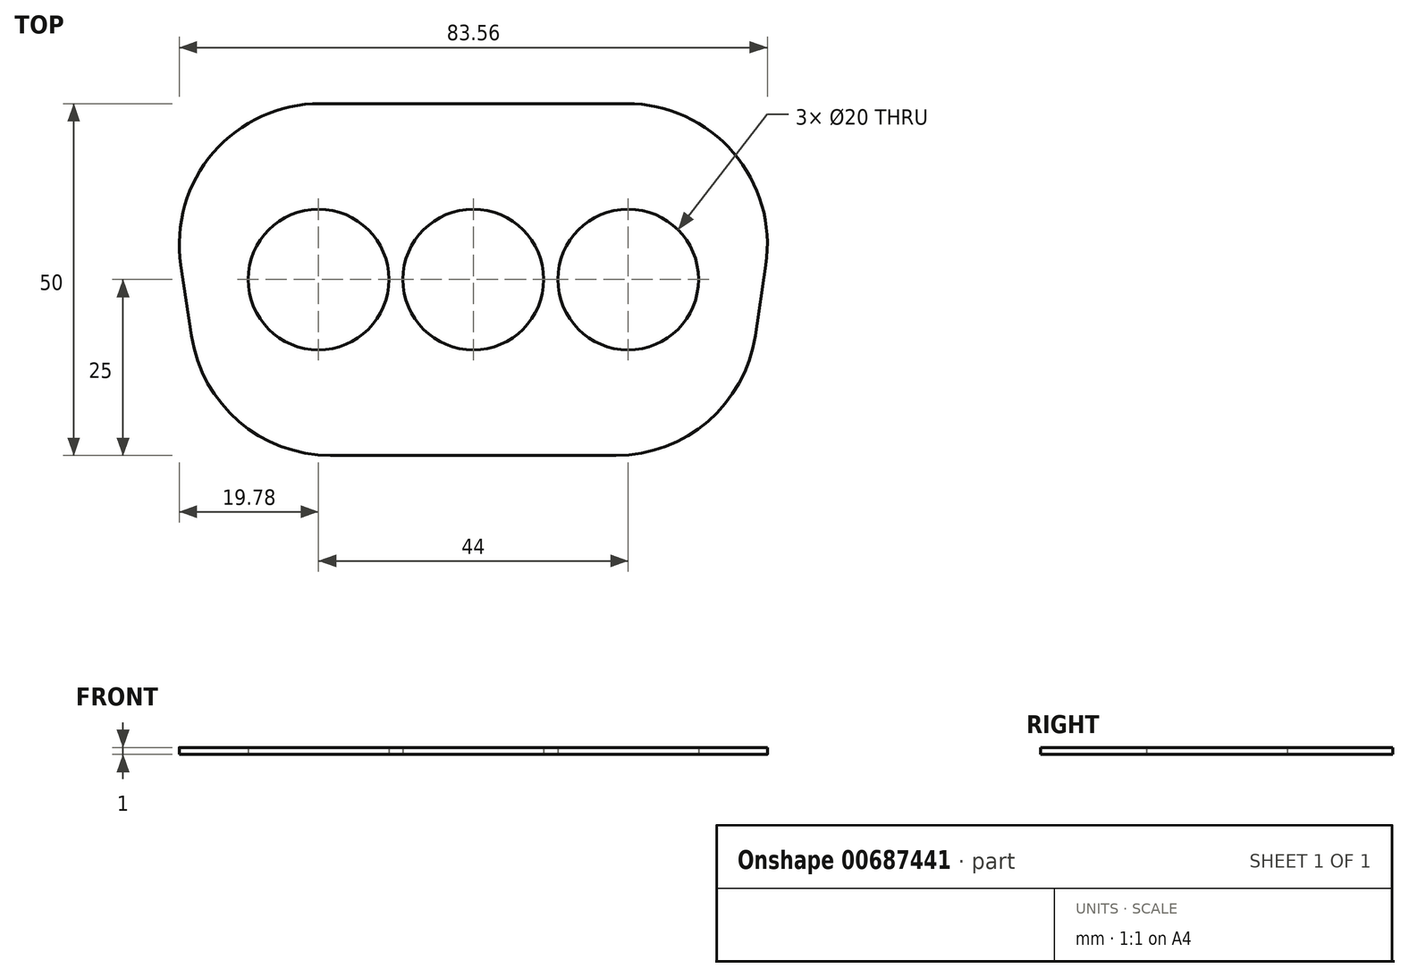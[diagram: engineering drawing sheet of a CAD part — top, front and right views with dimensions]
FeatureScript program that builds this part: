
annotation { "Feature Type Name" : "Feature", "Feature Type Description" : "" }
export const myFeature = defineFeature(function(context is Context, id is Id, definition is map)
    precondition{}
    {
        {
            var Q0;
            Q0=qCreatedBy(makeId("Top.planeOp"),FACE);
            var sketch = newSketch(context, id + "F0", { "sketchPlane" : qUnion([Q0])});
            skLineSegment(sketch, "E0", {"start": v(-45, 0) * mm, "end": v(45, 0) * mm});
            skLineSegment(sketch, "E1", {"start": v(-37.5, -50) * mm, "end": v(37.5, -50) * mm});
            skLineSegment(sketch, "E2", {"start": v(0, 0) * mm, "end": v(0, -50) * mm});
            skLineSegment(sketch, "E3", {"start": v(-45, 0) * mm, "end": v(-37.5, -50) * mm});
            skLineSegment(sketch, "E4", {"start": v(37.5, -50) * mm, "end": v(45, 0) * mm});
            skCircle(sketch, "E5", {"center": v(0, -25) * mm, "radius": 10 * mm});
            skCircle(sketch, "E6", {"center": v(-22, -25) * mm, "radius": 10 * mm});
            skCircle(sketch, "E7.MirrorC", {"center": v(22, -25) * mm, "radius": 10 * mm});
            skSolve(sketch);
        }
        {
            var Q0;
            Q0 = qSketchRegion(id + "F0", true);
            extrude(context, id + "F1", {"entities" : qUnion([Q0]), "depth" : 1 * mm, "offsetDistance" : 25 * mm});
        }
        {
            var Q0;
            Q0=makeQuery(id+"F1.opExtrude","SWEPT_EDGE",EDGE,{"disambiguationData":[OSD([sQuery(id+"F0.wireOp",EDGE,"E1"),sQuery(id+"F0.wireOp",EDGE,"E3")])]});
            var Q1;
            Q1=makeQuery(id+"F1.opExtrude","SWEPT_EDGE",EDGE,{"disambiguationData":[OSD([sQuery(id+"F0.wireOp",EDGE,"E1"),sQuery(id+"F0.wireOp",EDGE,"E4")])]});
            var Q2;
            Q2=makeQuery(id+"F1.opExtrude","SWEPT_EDGE",EDGE,{"disambiguationData":[OSD([sQuery(id+"F0.wireOp",EDGE,"E0"),sQuery(id+"F0.wireOp",EDGE,"E4")])]});
            var Q3;
            Q3=makeQuery(id+"F1.opExtrude","SWEPT_EDGE",EDGE,{"disambiguationData":[OSD([sQuery(id+"F0.wireOp",EDGE,"E0"),sQuery(id+"F0.wireOp",EDGE,"E3")])]});
            fillet(context, id + "F2", {"entities" : qUnion([Q0, Q1, Q2, Q3]), "radius" : 20 * mm, "tangentPropagation" : true, "allowEdgeOverflow" : false});
        }
    });
